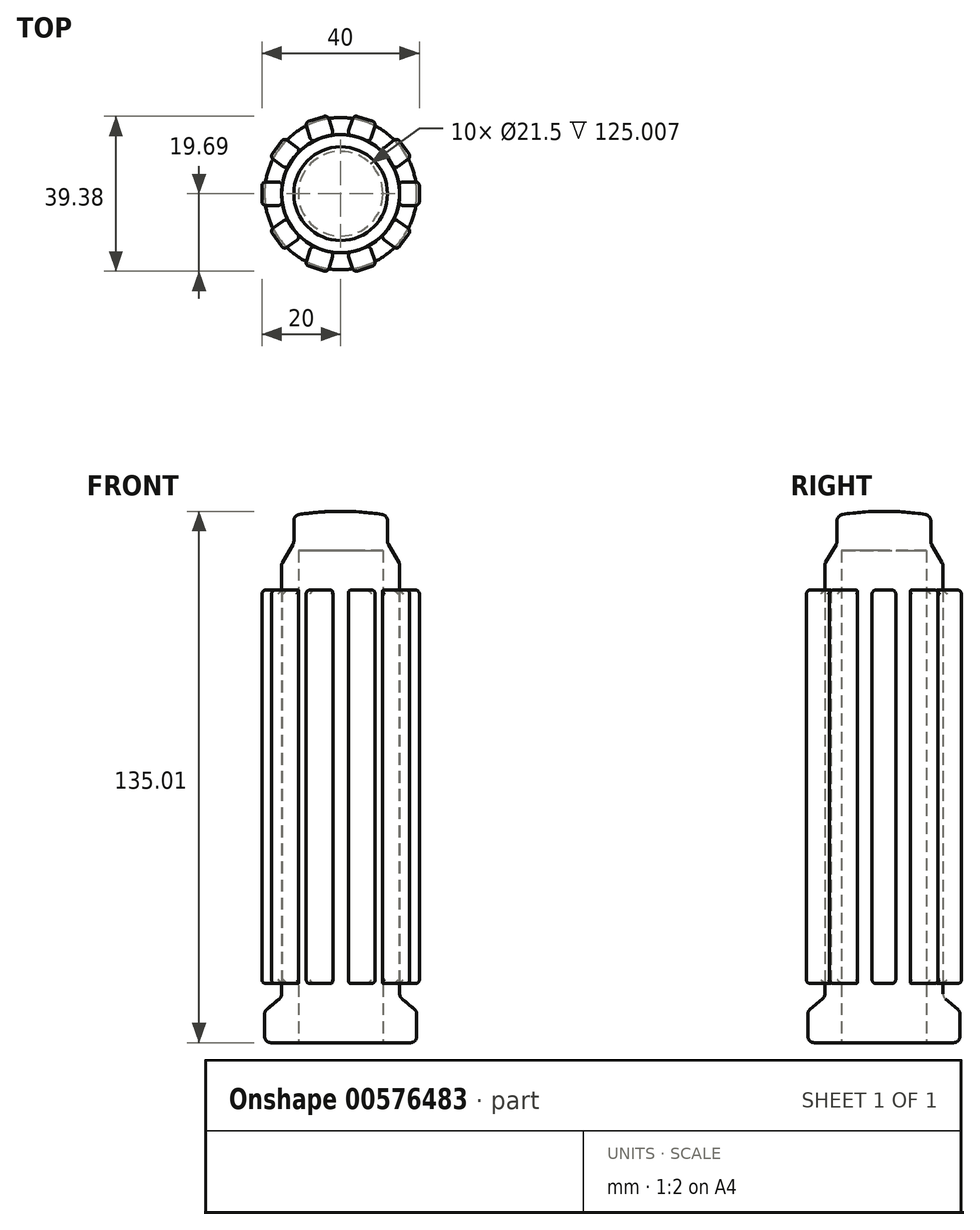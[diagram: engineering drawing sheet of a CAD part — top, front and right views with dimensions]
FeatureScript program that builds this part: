
annotation { "Feature Type Name" : "Feature", "Feature Type Description" : "" }
export const myFeature = defineFeature(function(context is Context, id is Id, definition is map)
    precondition{}
    {
        {
            var Q0;
            Q0=qCreatedBy(makeId("Front.planeOp"),FACE);
            var sketch = newSketch(context, id + "F0", { "sketchPlane" : qUnion([Q0])});
            skLineSegment(sketch, "E0", {"start": v(0, 135) * mm, "end": v(0, 125) * mm});
            skLineSegment(sketch, "E1", {"start": v(0, 125) * mm, "end": v(10.75, 125) * mm});
            skLineSegment(sketch, "E2", {"start": v(10.75, 125) * mm, "end": v(10.75, 0) * mm});
            skLineSegment(sketch, "E3", {"start": v(10.75, 0) * mm, "end": v(19.33, 0) * mm});
            skLineSegment(sketch, "E4", {"start": v(19.33, 0) * mm, "end": v(19.33, 8) * mm});
            skLineSegment(sketch, "E5", {"start": v(19.33, 8) * mm, "end": v(15, 11.62) * mm});
            skLineSegment(sketch, "E6", {"start": v(15, 11.62) * mm, "end": v(15, 121.62) * mm});
            skLineSegment(sketch, "E7", {"start": v(15, 121.62) * mm, "end": v(11.9, 127) * mm});
            skLineSegment(sketch, "E8", {"start": v(11.9, 127) * mm, "end": v(11.9, 133.95) * mm});
            skArc(sketch, "E9", {"start": v(11.9, 133.95) * mm, "mid": v(5.97, 134.74) * mm, "end": v(0, 135) * mm});
            skLineSegment(sketch, "E10", {"start": v(0, 0) * mm, "end": v(0, 210.8) * mm, "construction": true});
            skSolve(sketch);
        }
        {
            var Q0;
            Q0 = qSketchRegion(id + "F0", true);
            var Q1;
            Q1=sQuery(id+"F0.wireOp",EDGE,"E10");
            revolve(context, id + "F1", {"surfaceOperationType" : NewSurfaceOperationType.NEW, "entities" : qUnion([Q0]), "axis" : qUnion([Q1]), "revolveType" : RevolveType.FULL});
        }
        {
            var Q0;
            Q0=makeQuery(id+"F1.opRevolve","SWEPT_EDGE",EDGE,{"disambiguationData":[OSD([sQuery(id+"F0.wireOp",EDGE,"E8"),sQuery(id+"F0.wireOp",EDGE,"E9")])]});
            var Q1;
            Q1=makeQuery(id+"F1.opRevolve","SWEPT_EDGE",EDGE,{"disambiguationData":[OSD([sQuery(id+"F0.wireOp",EDGE,"E6"),sQuery(id+"F0.wireOp",EDGE,"E7")])]});
            var Q2;
            Q2=makeQuery(id+"F1.opRevolve","SWEPT_EDGE",EDGE,{"disambiguationData":[OSD([sQuery(id+"F0.wireOp",EDGE,"E7"),sQuery(id+"F0.wireOp",EDGE,"E8")])]});
            var Q3;
            Q3=makeQuery(id+"F1.opRevolve","SWEPT_EDGE",EDGE,{"disambiguationData":[OSD([sQuery(id+"F0.wireOp",EDGE,"E5"),sQuery(id+"F0.wireOp",EDGE,"E6")])]});
            var Q4;
            Q4=makeQuery(id+"F1.opRevolve","SWEPT_EDGE",EDGE,{"disambiguationData":[OSD([sQuery(id+"F0.wireOp",EDGE,"E4"),sQuery(id+"F0.wireOp",EDGE,"E5")])]});
            var Q5;
            Q5=makeQuery(id+"F1.opRevolve","SWEPT_EDGE",EDGE,{"disambiguationData":[OSD([sQuery(id+"F0.wireOp",EDGE,"E3"),sQuery(id+"F0.wireOp",EDGE,"E4")])]});
            fillet(context, id + "F2", {"entities" : qUnion([Q0, Q1, Q2, Q3, Q4, Q5]), "radius" : 1.6 * mm, "tangentPropagation" : true, "allowEdgeOverflow" : false});
        }
        {
            var Q0;
            Q0=qCreatedBy(makeId("Right.planeOp"),FACE);
            cPlane(context, id + "F3", {"entities" : qUnion([Q0]), "cplaneType" : CPlaneType.OFFSET, "offset" : 20 * mm, "width" : 150 * mm, "height" : 150 * mm});
        }
        {
            var Q0;
            Q0=qCreatedBy(id+"F3.planeOp",FACE);
            var sketch = newSketch(context, id + "F4", { "sketchPlane" : qUnion([Q0])});
            skLineSegment(sketch, "E11.bottom", {"start": v(-3, 15) * mm, "end": v(3, 15) * mm});
            skLineSegment(sketch, "E11.top", {"start": v(-3, 115) * mm, "end": v(3, 115) * mm});
            skLineSegment(sketch, "E11.left", {"start": v(-3, 15) * mm, "end": v(-3, 115) * mm});
            skLineSegment(sketch, "E11.right", {"start": v(3, 15) * mm, "end": v(3, 115) * mm});
            skSolve(sketch);
        }
        {
            var Q0;
            Q0 = qSketchRegion(id + "F4", true);
            var Q1;
            Q1=makeQuery(id+"F1.opRevolve","SWEPT_FACE",FACE,{"disambiguationData":[OSD([sQuery(id+"F0.wireOp",EDGE,"E6")])]});
            extrude(context, id + "F5", {"entities" : qUnion([Q0]), "endBound" : BoundingType.UP_TO_SURFACE, "oppositeDirection" : true, "depth" : 25 * mm, "endBoundEntityFace" : qUnion([Q1]), "offsetDistance" : 25 * mm});
        }
        {
            var Q0;
            Q0=makeQuery(id+"F5.opExtrude","CAP_FACE",FACE,{"disambiguationData":[OSD([sQuery(id+"F4.wireOp",EDGE,"E11.bottom"),sQuery(id+"F4.wireOp",EDGE,"E11.top"),sQuery(id+"F4.wireOp",EDGE,"E11.left"),sQuery(id+"F4.wireOp",EDGE,"E11.right")])],"isStart":true});
            var Q1;
            Q1=makeQuery(id+"F5.opExtrude","SWEPT_FACE",FACE,{"disambiguationData":[OSD([sQuery(id+"F4.wireOp",EDGE,"E11.right")])]});
            var Q2;
            Q2=makeQuery(id+"F5.opExtrude","SWEPT_FACE",FACE,{"disambiguationData":[OSD([sQuery(id+"F4.wireOp",EDGE,"E11.left")])]});
            fillet(context, id + "F6", {"entities" : qUnion([Q0, Q1, Q2]), "radius" : 1 * mm, "tangentPropagation" : true, "allowEdgeOverflow" : false});
        }
        {
            var Q0;
            Q0=makeQuery(id+"F5.opExtrude","SWEPT_BODY",BODY,{"disambiguationData":[OSD([sQuery(id+"F4.wireOp",EDGE,"E11.bottom"),sQuery(id+"F4.wireOp",EDGE,"E11.top"),sQuery(id+"F4.wireOp",EDGE,"E11.left"),sQuery(id+"F4.wireOp",EDGE,"E11.right")])]});
            var Q1;
            Q1=makeQuery(id+"F1.opRevolve","SWEPT_BODY",BODY,{"disambiguationData":[OSD([sQuery(id+"F0.wireOp",EDGE,"E0"),sQuery(id+"F0.wireOp",EDGE,"E1"),sQuery(id+"F0.wireOp",EDGE,"E2"),sQuery(id+"F0.wireOp",EDGE,"E3"),sQuery(id+"F0.wireOp",EDGE,"E4"),sQuery(id+"F0.wireOp",EDGE,"E5"),sQuery(id+"F0.wireOp",EDGE,"E6"),sQuery(id+"F0.wireOp",EDGE,"E7"),sQuery(id+"F0.wireOp",EDGE,"E8"),sQuery(id+"F0.wireOp",EDGE,"E9")])]});
            var Q2;
            Q2=makeQuery(id+"F1.opRevolve","SWEPT_FACE",FACE,{"disambiguationData":[OSD([sQuery(id+"F0.wireOp",EDGE,"E6")])]});
            circularPattern(context, id + "F7", {"entities" : qUnion([Q0, Q1]), "axis" : qUnion([Q2]), "angle" : 360 * degree, "instanceCount" : 10, "oppositeDirection" : true, "equalSpace" : true});
        }
    });
